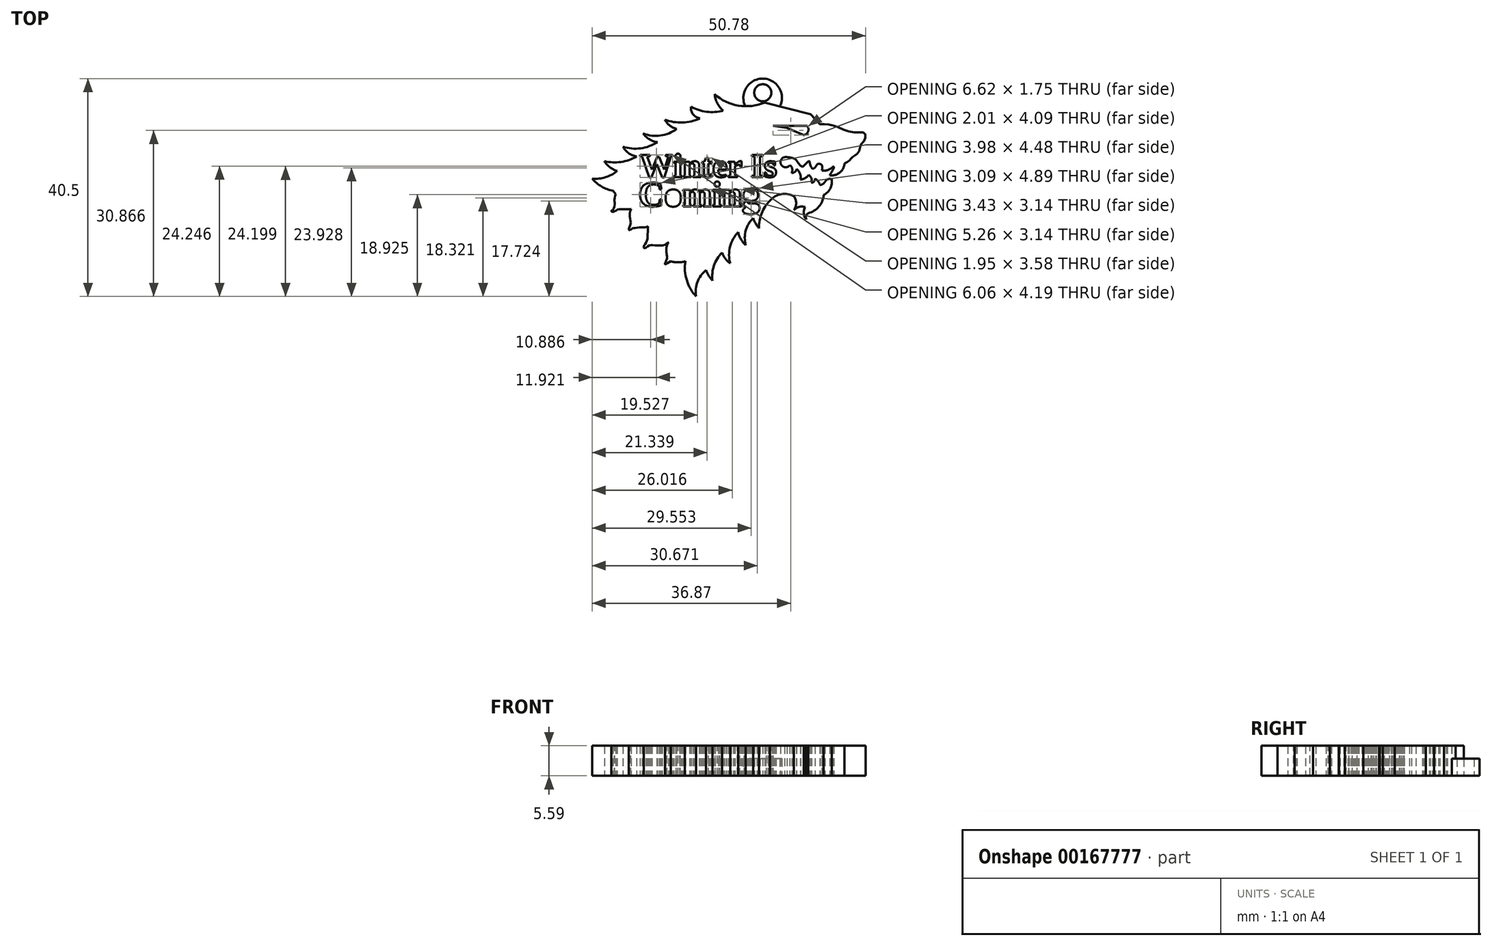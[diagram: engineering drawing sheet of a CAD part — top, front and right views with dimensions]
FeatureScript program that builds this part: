
annotation { "Feature Type Name" : "Feature", "Feature Type Description" : "" }
export const myFeature = defineFeature(function(context is Context, id is Id, definition is map)
    precondition{}
    {
        {
            var Q0;
            Q0=qCreatedBy(makeId("Top.planeOp"),FACE);
            var sketch = newSketch(context, id + "F0", { "sketchPlane" : qUnion([Q0])});
            skArc(sketch, "E0", {"start": v(-3.8, 20.04) * mm, "mid": v(0.63, 17.93) * mm, "end": v(5.5, 18.5) * mm});
            skArc(sketch, "E1", {"start": v(-8.2, 17.73) * mm, "mid": v(-5.28, 16.79) * mm, "end": v(-2.21, 16.97) * mm});
            skArc(sketch, "E2", {"start": v(-13.03, 15.3) * mm, "mid": v(-9.76, 14.79) * mm, "end": v(-6.55, 15.55) * mm});
            skArc(sketch, "E3", {"start": v(-17.05, 12.74) * mm, "mid": v(-13.84, 12.37) * mm, "end": v(-10.85, 13.6) * mm});
            skArc(sketch, "E4", {"start": v(-20.82, 10.29) * mm, "mid": v(-17.53, 10) * mm, "end": v(-14.42, 11.12) * mm});
            skArc(sketch, "E5", {"start": v(-24.27, 7.6) * mm, "mid": v(-21.2, 7.46) * mm, "end": v(-18.3, 8.46) * mm});
            skArc(sketch, "E6", {"start": v(-26.54, 4.36) * mm, "mid": v(-24.08, 4.6) * mm, "end": v(-21.91, 5.78) * mm});
            skLineSegment(sketch, "E7", {"start": v(5.5, 18.5) * mm, "end": v(14.05, 16.3) * mm});
            skLineSegment(sketch, "E8", {"start": v(14.05, 16.3) * mm, "end": v(15.78, 14.5) * mm});
            skFitSpline(sketch, "E9", {"points": [v(15.78, 14.5) * mm, v(18.25, 14.23) * mm, v(21.8, 13) * mm, v(24.09, 12.78) * mm, v(24, 11.42) * mm, v(23.35, 10.61) * mm, v(23.1, 9.63) * mm, v(22.37, 8.7) * mm, v(21.72, 8.27) * mm, v(21.28, 7.73) * mm, v(20.33, 7.16) * mm], "startDerivative": vector(18.27, 0.08) * mm, "endDerivative": vector(-12.36, -6.01) * mm});
            skArc(sketch, "E10", {"start": v(17.57, 4.97) * mm, "mid": v(19.43, 5.46) * mm, "end": v(20.33, 7.16) * mm});
            skArc(sketch, "E11", {"start": v(16.16, 5.83) * mm, "mid": v(17.29, 5.96) * mm, "end": v(18.23, 6.6) * mm});
            skFitSpline(sketch, "E12", {"points": [v(18.23, 6.6) * mm, v(18.35, 6.49) * mm, v(17.57, 4.97) * mm], "startDerivative": vector(0.69, -0.3) * mm, "endDerivative": vector(-1.6, -2.56) * mm});
            skFitSpline(sketch, "E13", {"points": [v(16.16, 5.83) * mm, v(16.16, 6.81) * mm, v(16, 6.97) * mm, v(15.54, 7.14) * mm, v(15.19, 6.86) * mm, v(14.47, 6.2) * mm, v(14.06, 6.73) * mm, v(13.82, 7.62) * mm], "startDerivative": vector(0.52, 6.87) * mm, "endDerivative": vector(-1.12, 5.13) * mm});
            skFitSpline(sketch, "E14", {"points": [v(13.82, 7.62) * mm, v(13.3, 7.31) * mm, v(12.53, 6.6) * mm, v(11.36, 7.84) * mm], "startDerivative": vector(-2.05, -0.77) * mm, "endDerivative": vector(-2.9, 4.54) * mm});
            skArc(sketch, "E15", {"start": v(9.19, 8.35) * mm, "mid": v(8.54, 7.82) * mm, "end": v(8.55, 6.99) * mm});
            skArc(sketch, "E16", {"start": v(8.55, 6.99) * mm, "mid": v(9.32, 6.46) * mm, "end": v(10.17, 6.84) * mm});
            skArc(sketch, "E17", {"start": v(10.53, 5.42) * mm, "mid": v(10.61, 6.2) * mm, "end": v(10.17, 6.84) * mm});
            skArc(sketch, "E18", {"start": v(10.53, 5.42) * mm, "mid": v(11.12, 5.6) * mm, "end": v(11.43, 6.13) * mm});
            skArc(sketch, "E19", {"start": v(12.14, 4.22) * mm, "mid": v(12.08, 5.28) * mm, "end": v(11.43, 6.13) * mm});
            skArc(sketch, "E20", {"start": v(12.14, 4.22) * mm, "mid": v(13.02, 4.42) * mm, "end": v(13.65, 5.05) * mm});
            skArc(sketch, "E21", {"start": v(14.2, 3.6) * mm, "mid": v(14.17, 4.42) * mm, "end": v(13.65, 5.05) * mm});
            skArc(sketch, "E22", {"start": v(14.2, 3.6) * mm, "mid": v(14.7, 3.83) * mm, "end": v(14.83, 4.37) * mm});
            skArc(sketch, "E23", {"start": v(15.81, 3.15) * mm, "mid": v(15.42, 3.84) * mm, "end": v(14.83, 4.37) * mm});
            skArc(sketch, "E24", {"start": v(15.81, 3.15) * mm, "mid": v(16.32, 3.36) * mm, "end": v(16.7, 3.76) * mm});
            skArc(sketch, "E25", {"start": v(17.96, 4.26) * mm, "mid": v(17.24, 4.24) * mm, "end": v(16.7, 3.76) * mm});
            skArc(sketch, "E26", {"start": v(16.46, 1.32) * mm, "mid": v(17.7, 2.54) * mm, "end": v(17.96, 4.26) * mm});
            skArc(sketch, "E27", {"start": v(13.58, -2.08) * mm, "mid": v(15.57, -0.85) * mm, "end": v(16.46, 1.32) * mm});
            skArc(sketch, "E28", {"start": v(13.58, -2.08) * mm, "mid": v(13.21, -2.54) * mm, "end": v(13.22, -3.13) * mm});
            skArc(sketch, "E29", {"start": v(13.01, -0.94) * mm, "mid": v(12.78, -2.12) * mm, "end": v(13.22, -3.24) * mm});
            skArc(sketch, "E30", {"start": v(13.01, -0.94) * mm, "mid": v(11.9, -0.9) * mm, "end": v(10.95, -1.48) * mm});
            skArc(sketch, "E31", {"start": v(10.95, -1.48) * mm, "mid": v(11.35, -0.2) * mm, "end": v(10.95, 1.08) * mm});
            skArc(sketch, "E32", {"start": v(10.95, 1.08) * mm, "mid": v(8.58, 1.46) * mm, "end": v(6.5, 0.27) * mm});
            skArc(sketch, "E33", {"start": v(6.5, 0.27) * mm, "mid": v(4.94, -2.08) * mm, "end": v(4.44, -4.86) * mm});
            skArc(sketch, "E34", {"start": v(3.37, -2.96) * mm, "mid": v(3.81, -3.96) * mm, "end": v(4.44, -4.86) * mm});
            skArc(sketch, "E35", {"start": v(3.37, -2.96) * mm, "mid": v(2, -5.29) * mm, "end": v(1.99, -7.99) * mm});
            skArc(sketch, "E36", {"start": v(0.58, -5.59) * mm, "mid": v(1.09, -6.9) * mm, "end": v(1.99, -7.99) * mm});
            skArc(sketch, "E37", {"start": v(0.58, -5.59) * mm, "mid": v(-0.93, -8.29) * mm, "end": v(-0.91, -11.38) * mm});
            skArc(sketch, "E38", {"start": v(-2.43, -9.4) * mm, "mid": v(-1.82, -10.51) * mm, "end": v(-0.91, -11.38) * mm});
            skArc(sketch, "E39", {"start": v(-2.43, -9.4) * mm, "mid": v(-3.92, -11.8) * mm, "end": v(-4.18, -14.6) * mm});
            skArc(sketch, "E40", {"start": v(-5.4, -12.66) * mm, "mid": v(-4.88, -13.7) * mm, "end": v(-4.18, -14.6) * mm});
            skArc(sketch, "E41", {"start": v(-5.4, -12.66) * mm, "mid": v(-6.98, -14.86) * mm, "end": v(-7.22, -17.55) * mm});
            skArc(sketch, "E42", {"start": v(-9.22, -11) * mm, "mid": v(-8.98, -14.5) * mm, "end": v(-7.22, -17.55) * mm});
            skArc(sketch, "E43", {"start": v(-11.95, -11) * mm, "mid": v(-10.59, -11.2) * mm, "end": v(-9.22, -11) * mm});
            skFitSpline(sketch, "E44", {"points": [v(-11.95, -11) * mm, v(-13.03, -11.55) * mm, v(-12.66, -10.6) * mm, v(-12.69, -9.72) * mm, v(-12.72, -8.29) * mm, v(-12.33, -7.46) * mm], "startDerivative": vector(-7.2, -4.75) * mm, "endDerivative": vector(2.56, 3.95) * mm});
            skFitSpline(sketch, "E45", {"points": [v(-12.33, -7.46) * mm, v(-13.27, -8) * mm, v(-14.56, -8.06) * mm, v(-15.6, -8.03) * mm, v(-16.14, -8.17) * mm, v(-16.85, -8.58) * mm, v(-16.95, -8.22) * mm, v(-16.62, -7.7) * mm, v(-16.31, -7) * mm, v(-16.23, -5.97) * mm, v(-16.17, -4.54) * mm], "startDerivative": vector(-7.84, -5.9) * mm, "endDerivative": vector(0.51, 11.58) * mm});
            skFitSpline(sketch, "E46", {"points": [v(-16.17, -4.54) * mm, v(-16.87, -4.72) * mm, v(-17.7, -4.7) * mm, v(-18.63, -4.83) * mm, v(-19.1, -4.93) * mm, v(-19.65, -5.22) * mm, v(-19.7, -4.83) * mm, v(-19.4, -3.95) * mm, v(-19.52, -3.02) * mm, v(-19.44, -1.57) * mm, v(-19.3, -1.27) * mm], "startDerivative": vector(-6.89, -2.48) * mm, "endDerivative": vector(2.23, 3.29) * mm});
            skFitSpline(sketch, "E47", {"points": [v(-19.3, -1.27) * mm, v(-20.67, -1.34) * mm, v(-21.67, -1.34) * mm, v(-22.42, -1.72) * mm, v(-22.93, -1.78) * mm, v(-22.93, -1.54) * mm, v(-22.62, -1.34) * mm, v(-22.35, -0.23) * mm, v(-22.42, 0.45) * mm, v(-22.15, 1.49) * mm], "startDerivative": vector(-9.47, -0.92) * mm, "endDerivative": vector(2.96, 8.53) * mm});
            skArc(sketch, "E48", {"start": v(-26.54, 4.36) * mm, "mid": v(-24.79, 2.88) * mm, "end": v(-22.65, 2.08) * mm});
            skLineSegment(sketch, "E49", {"start": v(13.35, 14.19) * mm, "end": v(7.02, 14.19) * mm});
            skLineSegment(sketch, "E50", {"start": v(7.02, 14.19) * mm, "end": v(9.68, 13.78) * mm});
            skLineSegment(sketch, "E51", {"start": v(9.68, 13.78) * mm, "end": v(12.77, 12.44) * mm});
            skArc(sketch, "E52", {"start": v(12.77, 12.44) * mm, "mid": v(13.59, 13.14) * mm, "end": v(13.35, 14.19) * mm});
            skArc(sketch, "E53", {"start": v(-3.8, 20.04) * mm, "mid": v(-3.28, 18.36) * mm, "end": v(-2.21, 16.97) * mm});
            skArc(sketch, "E54", {"start": v(-8.2, 17.73) * mm, "mid": v(-7.8, 16.32) * mm, "end": v(-6.55, 15.55) * mm});
            skArc(sketch, "E55", {"start": v(-13.03, 15.3) * mm, "mid": v(-12.13, 14.2) * mm, "end": v(-10.85, 13.6) * mm});
            skArc(sketch, "E56", {"start": v(-17.05, 12.74) * mm, "mid": v(-15.9, 11.66) * mm, "end": v(-14.42, 11.12) * mm});
            skArc(sketch, "E57", {"start": v(-20.82, 10.29) * mm, "mid": v(-19.76, 9.1) * mm, "end": v(-18.3, 8.46) * mm});
            skArc(sketch, "E58", {"start": v(-24.27, 7.6) * mm, "mid": v(-23.26, 6.47) * mm, "end": v(-21.91, 5.78) * mm});
            skText(sketch, "E59", { "text": "Winter Is", "fontName": "Tinos-Bold.ttf"});
            skText(sketch, "E60", { "text": "Coming", "fontName": "Tinos-Bold.ttf"});
            skArc(sketch, "E61", {"start": v(8.35, 17.77) * mm, "mid": v(5.16, 22.95) * mm, "end": v(1.9, 17.8) * mm});
            skCircle(sketch, "E62", {"center": v(5.16, 20.32) * mm, "radius": 1.59 * mm});
            skPoint(sketch, "E62.centerSnap0", {"position": v(5.16, 22.95) * mm});
            skFitSpline(sketch, "E63", {"points": [v(9.19, 8.35) * mm, v(11.36, 7.84) * mm], "startDerivative": vector(2.58, 0.11) * mm, "endDerivative": vector(1.64, -1.19) * mm});
            skLineSegment(sketch, "E64", {"start": v(-22.65, 2.08) * mm, "end": v(-22.15, 1.49) * mm});
            skLineSegment(sketch, "E65", {"start": v(13.22, -3.13) * mm, "end": v(13.22, -3.24) * mm});
            const initialGuessF0  = {"E59": [-0.01774, 0.00465, 1, 0, 0.0045], "E60": [-0.01797, -0.0008, 1, 0, 0.0048]};
            skSetInitialGuess(sketch, initialGuessF0);
            skSolve(sketch);
        }
        {
            var Q0;
            Q0=makeQuery(id+"F0.imprint","IMPRINT",FACE,{"disambiguationData":[TD([[makeQuery(id+"F0.imprint","IMPRINT",EDGE,{"derivedFrom":sQuery(id+"F0.wireOp",EDGE,"E1")}),-1.0]])]});
            extrude(context, id + "F1", {"entities" : qUnion([Q0]), "depth" : 5.6 * mm});
        }
        {
            var Q0;
            {var subQ3=sQuery(id+"F0.wireOp",EDGE,"E61");Q0=makeQuery(id+"F0.imprint","IMPRINT",FACE,{"disambiguationData":[TD([[makeQuery(id+"F0.imprint","IMPRINT",EDGE,{"derivedFrom":subQ3}),1.0]])]});}
            extrude(context, id + "F2", {"entities" : qUnion([Q0]), "operationType" : NewBodyOperationType.ADD, "depth" : 3.17 * mm});
        }
    });
